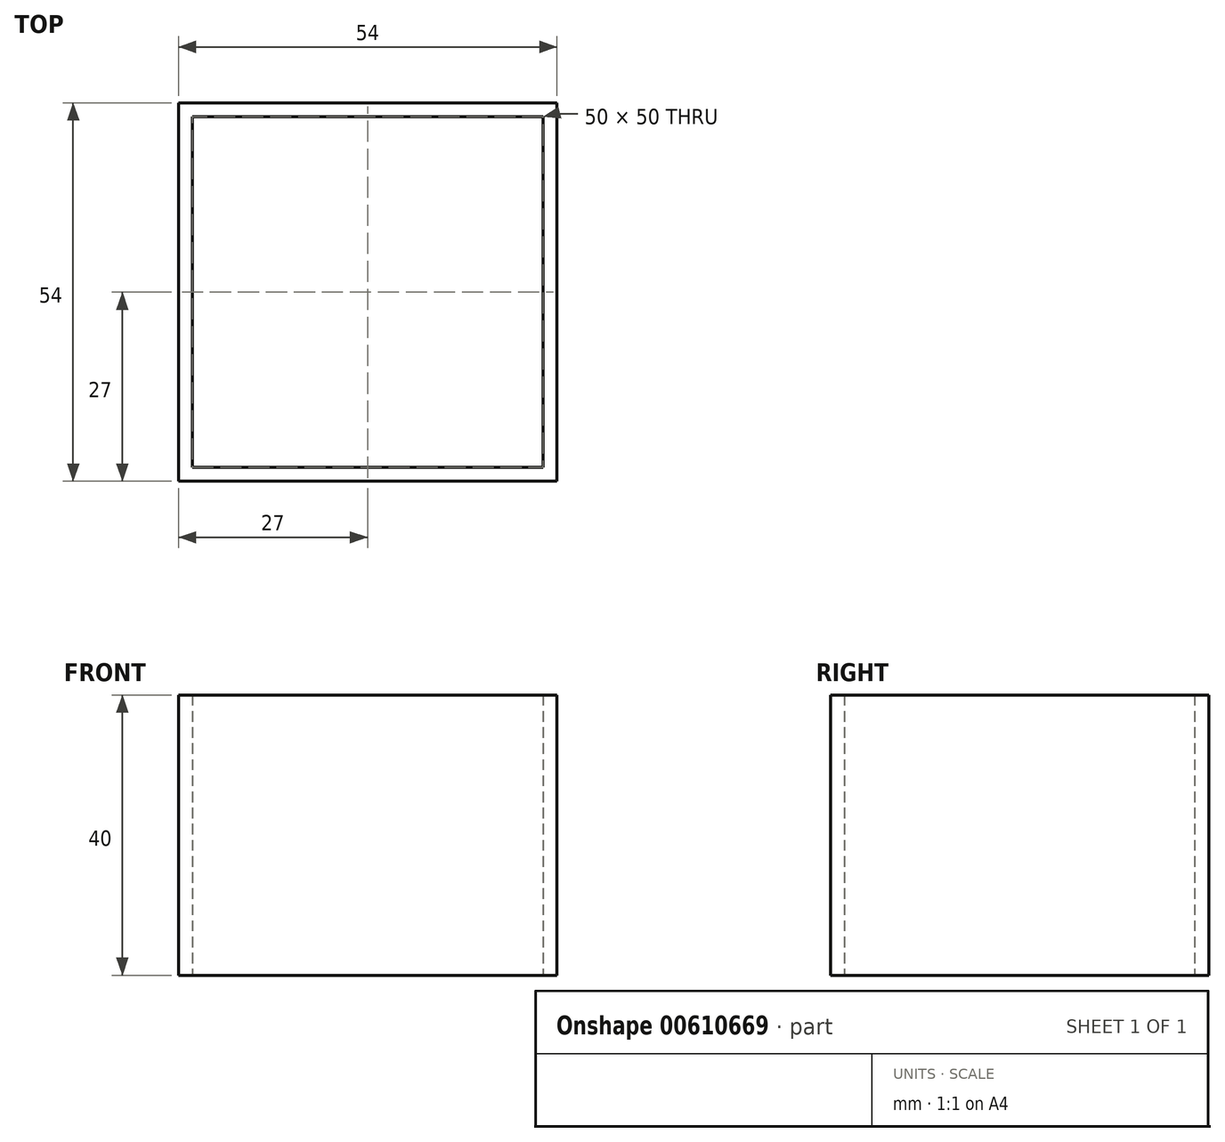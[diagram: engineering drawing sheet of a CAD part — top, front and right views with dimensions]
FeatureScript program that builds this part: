
annotation { "Feature Type Name" : "Feature", "Feature Type Description" : "" }
export const myFeature = defineFeature(function(context is Context, id is Id, definition is map)
    precondition{}
    {
        {
            var Q0;
            Q0=qCreatedBy(makeId("Top.planeOp"),FACE);
            var sketch = newSketch(context, id + "F0", { "sketchPlane" : qUnion([Q0])});
            skLineSegment(sketch, "E0.bottom", {"start": v(25, 25) * mm, "end": v(-25, 25) * mm});
            skLineSegment(sketch, "E0.top", {"start": v(25, -25) * mm, "end": v(-25, -25) * mm});
            skLineSegment(sketch, "E0.left", {"start": v(25, 25) * mm, "end": v(25, -25) * mm});
            skLineSegment(sketch, "E0.right", {"start": v(-25, 25) * mm, "end": v(-25, -25) * mm});
            skPoint(sketch, "E0.middle", {"position": v(0, 0) * mm});
            skLineSegment(sketch, "E1.0", {"start": v(27, 27) * mm, "end": v(-27, 27) * mm});
            skLineSegment(sketch, "E1.1", {"start": v(27, 27) * mm, "end": v(27, -27) * mm});
            skLineSegment(sketch, "E1.2", {"start": v(27, -27) * mm, "end": v(-27, -27) * mm});
            skLineSegment(sketch, "E1.3", {"start": v(-27, 27) * mm, "end": v(-27, -27) * mm});
            skSolve(sketch);
        }
        {
            var Q0;
            Q0=makeQuery(id+"F0.imprint","IMPRINT",FACE,{"disambiguationData":[TD([[makeQuery(id+"F0.imprint","IMPRINT",EDGE,{"derivedFrom":sQuery(id+"F0.wireOp",EDGE,"E0.bottom")}),-1.0]])]});
            extrude(context, id + "F1", {"entities" : qUnion([Q0]), "depth" : 40 * mm, "offsetDistance" : 25 * mm});
        }
    });
